# Revit family: Table-Casual-Naughtone-Fold_Bar_2000
name_source: partatom
category: Furniture
revit_build: Autodesk Revit 2014 (Build: 20140709_2115(x64)
units: mm (PartAtom-declared; Revit-internal decimal feet)

## types (1)
- FOLD-BAR-2000
    Additional Materials = Additional material and finish options available. Please contact Naughtone direct for further information.
    AssetIdentifier = FOLD-BAR-2000
    Barcode = 0
    Base Option = Table and Bench Set available with RAL colour powder coated base.
    COBie Description = Designed by Naughtone, Fold tables and benches provide a simple surface with maximum clearance for legs, chairs and fresh air to fit underneath! The folded steel frame is proportioned carefully and finished beautifully making a low statement product to be used with any chair or as a bench and table set in any environment.
    Cost = 0 $
    Current Revision = 1
    Depth = 650 mm  [stored 2.13255 ft]
    Description = Fold Bar Table
    Height = 1000 mm  [stored 3.28084 ft]
    Length = 2000 mm  [stored 6.56168 ft]
    Manufacturer = Naughtone
    Model = Fold Bar Table
    Name = Furniture-Table-Casual-Naughtone-Fold
    Product Code = FOLD-BAR-2000
    Product URL = http://www.naughtone.com
    SerialNumber = 0
    TagNumber = 0
    Type Comments = Fold Bar Table
    TypeName = 2000mmx650mmx1000mm, Fold Bar Table
    URL = http://www.naughtone.com
    Uniclass = Pr_40_50_21_21
    WarrantyDuration = 60

note: [stored X ft] marks values corroborated as IEEE doubles in the binary element streams (Revit-internal decimal feet)

## geometry (parser evidence)
native form markers: Blend x1, Sweep x5
no freeform markers — native parametric forms only
